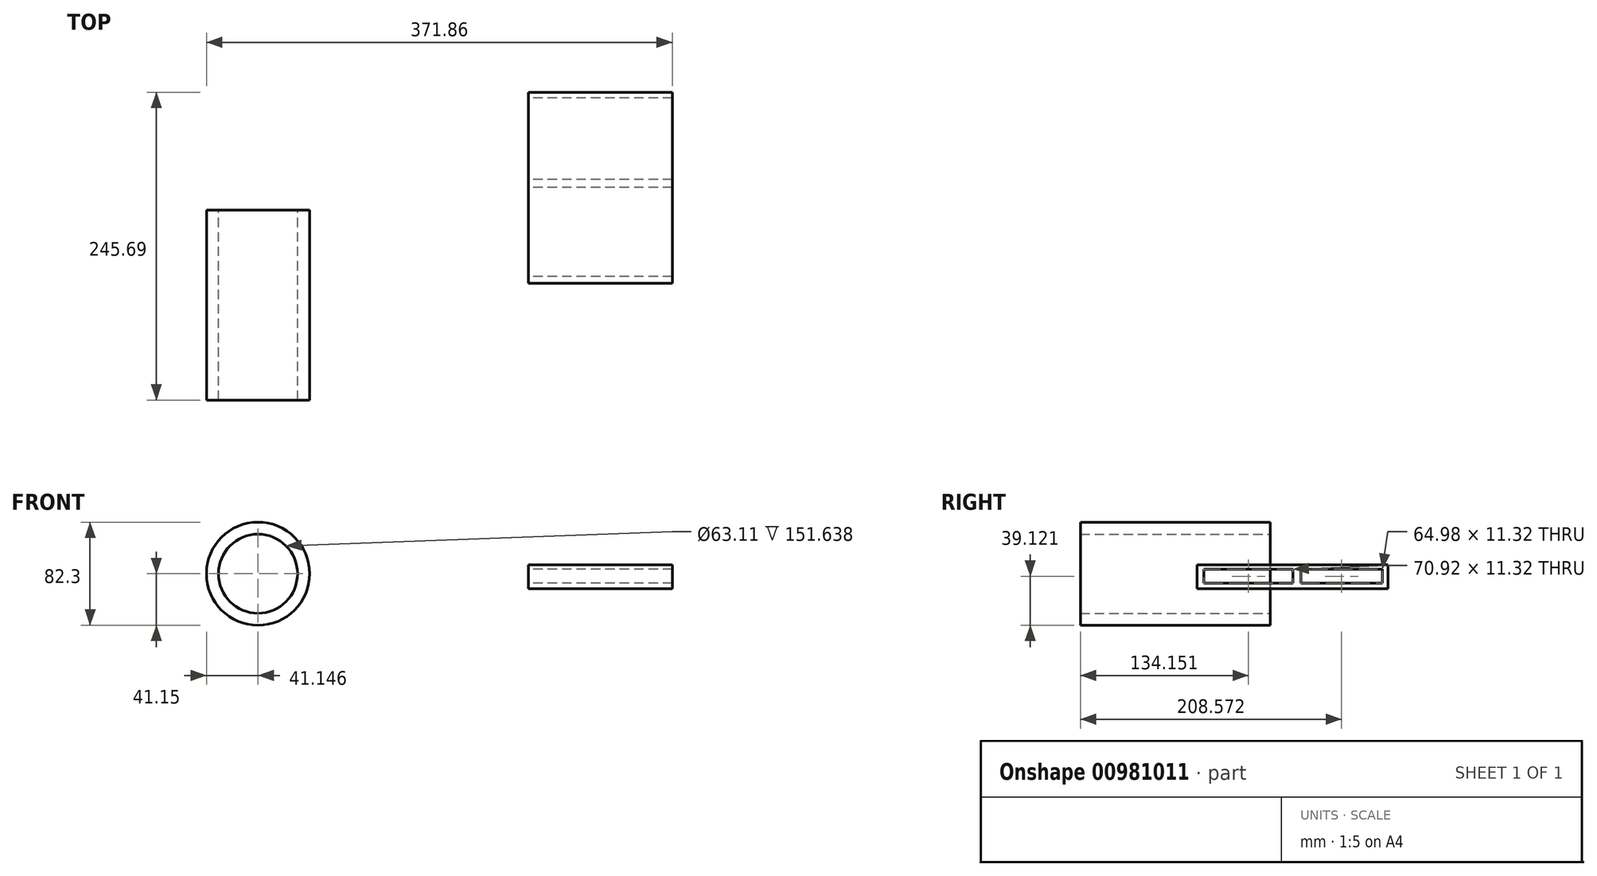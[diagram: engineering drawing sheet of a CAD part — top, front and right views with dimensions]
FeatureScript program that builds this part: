
annotation { "Feature Type Name" : "Feature", "Feature Type Description" : "" }
export const myFeature = defineFeature(function(context is Context, id is Id, definition is map)
    precondition{}
    {
        {
            var Q0;
            Q0=qCreatedBy(makeId("Front.planeOp"),FACE);
            var sketch = newSketch(context, id + "F0", { "sketchPlane" : qUnion([Q0])});
            skCircle(sketch, "E0", {"center": v(-215.9, 54.04) * mm, "radius": 41.15 * mm});
            skCircle(sketch, "E1", {"center": v(-215.9, 54.04) * mm, "radius": 31.56 * mm});
            skSolve(sketch);
        }
        {
            var Q0;
            Q0=makeQuery(id+"F0.imprint","IMPRINT",FACE,{"disambiguationData":[TD([[makeQuery(id+"F0.imprint","IMPRINT",EDGE,{"derivedFrom":sQuery(id+"F0.wireOp",EDGE,"E0")}),1.0]])]});
            extrude(context, id + "F1", {"entities" : qUnion([Q0]), "depth" : 151.64 * mm, "offsetDistance" : 25.4 * mm});
        }
        {
            var Q0;
            Q0=qCreatedBy(makeId("Right.planeOp"),FACE);
            var sketch = newSketch(context, id + "F2", { "sketchPlane" : qUnion([Q0])});
            skLineSegment(sketch, "E2.bottom", {"start": v(94.05, 42.16) * mm, "end": v(-58.35, 42.16) * mm});
            skLineSegment(sketch, "E2.top", {"start": v(94.05, 61.2) * mm, "end": v(-58.35, 61.2) * mm});
            skLineSegment(sketch, "E2.left", {"start": v(94.05, 42.16) * mm, "end": v(94.05, 61.2) * mm});
            skLineSegment(sketch, "E2.right", {"start": v(-58.35, 42.16) * mm, "end": v(-58.35, 61.2) * mm});
            skLineSegment(sketch, "E3.bottom", {"start": v(-52.95, 57.67) * mm, "end": v(17.97, 57.67) * mm});
            skLineSegment(sketch, "E3.top", {"start": v(-52.95, 46.35) * mm, "end": v(17.97, 46.35) * mm});
            skLineSegment(sketch, "E3.left", {"start": v(-52.95, 57.67) * mm, "end": v(-52.95, 46.35) * mm});
            skLineSegment(sketch, "E3.right", {"start": v(17.97, 57.67) * mm, "end": v(17.97, 46.35) * mm});
            skLineSegment(sketch, "E4.bottom", {"start": v(24.44, 57.67) * mm, "end": v(89.42, 57.67) * mm});
            skLineSegment(sketch, "E4.top", {"start": v(24.44, 46.35) * mm, "end": v(89.42, 46.35) * mm});
            skLineSegment(sketch, "E4.left", {"start": v(24.44, 57.67) * mm, "end": v(24.44, 46.35) * mm});
            skLineSegment(sketch, "E4.right", {"start": v(89.42, 57.67) * mm, "end": v(89.42, 46.35) * mm});
            skSolve(sketch);
        }
        {
            var Q0;
            Q0=makeQuery(id+"F2.imprint","IMPRINT",FACE,{"disambiguationData":[TD([[makeQuery(id+"F2.imprint","IMPRINT",EDGE,{"derivedFrom":sQuery(id+"F2.wireOp",EDGE,"E2.bottom")}),-1.0]])]});
            extrude(context, id + "F3", {"entities" : qUnion([Q0]), "depth" : 114.8 * mm, "offsetDistance" : 25.4 * mm});
        }
    });
